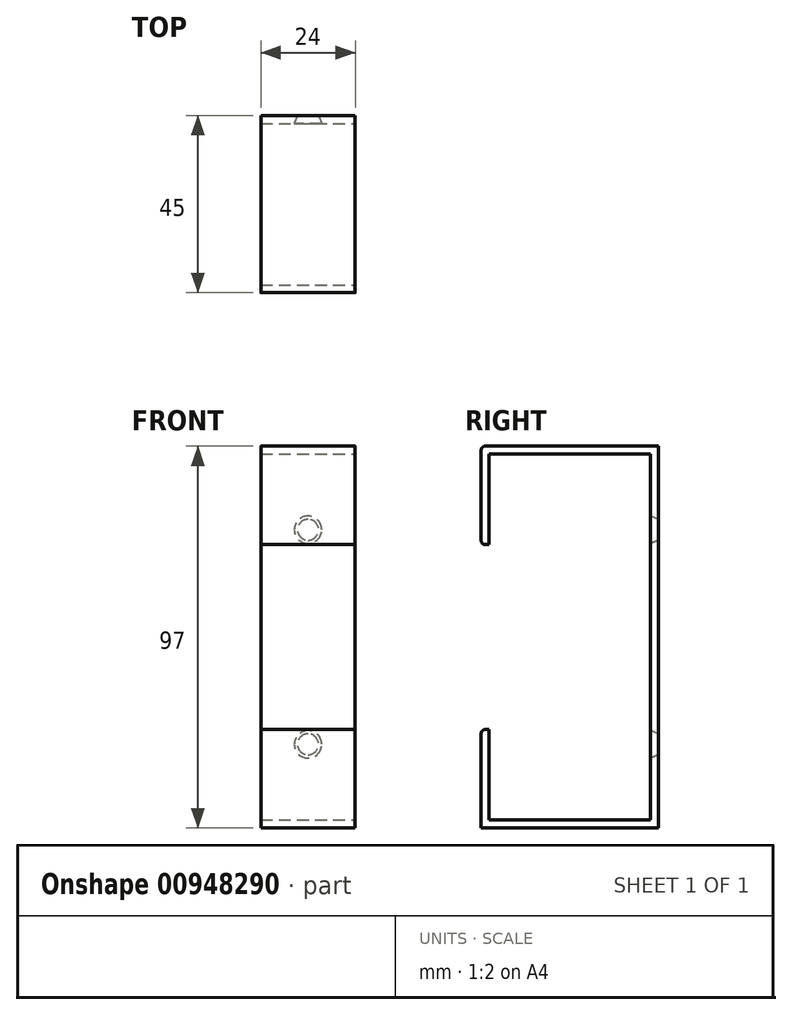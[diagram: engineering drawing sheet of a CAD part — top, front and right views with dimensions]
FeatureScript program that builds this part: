
annotation { "Feature Type Name" : "Feature", "Feature Type Description" : "" }
export const myFeature = defineFeature(function(context is Context, id is Id, definition is map)
    precondition{}
    {
        {
            var Q0;
            Q0=qCreatedBy(makeId("Top.planeOp"),FACE);
            var sketch = newSketch(context, id + "F0", { "sketchPlane" : qUnion([Q0])});
            skLineSegment(sketch, "E0.bottom", {"start": v(-14.15, 20.5) * mm, "end": v(7.85, 20.5) * mm});
            skLineSegment(sketch, "E0.top", {"start": v(-14.15, -20.5) * mm, "end": v(7.85, -20.5) * mm});
            skLineSegment(sketch, "E0.left", {"start": v(-14.15, 20.5) * mm, "end": v(-14.15, -20.5) * mm});
            skLineSegment(sketch, "E0.right", {"start": v(7.85, 20.5) * mm, "end": v(7.85, -20.5) * mm});
            skLineSegment(sketch, "E1.0", {"start": v(-14.15, 22.5) * mm, "end": v(7.85, 22.5) * mm});
            skLineSegment(sketch, "E2", {"start": v(-14.15, 22.5) * mm, "end": v(-14.15, 20.5) * mm});
            skLineSegment(sketch, "E3.0", {"start": v(9.85, 20.5) * mm, "end": v(9.85, -20.5) * mm});
            skLineSegment(sketch, "E4", {"start": v(7.85, 22.5) * mm, "end": v(9.85, 22.5) * mm});
            skLineSegment(sketch, "E5", {"start": v(9.85, 22.5) * mm, "end": v(9.85, 20.5) * mm});
            skLineSegment(sketch, "E6.0", {"start": v(-14.15, -22.5) * mm, "end": v(7.85, -22.5) * mm});
            skLineSegment(sketch, "E7", {"start": v(-14.15, -20.5) * mm, "end": v(-14.15, -22.5) * mm});
            skLineSegment(sketch, "E8", {"start": v(7.85, -22.5) * mm, "end": v(9.85, -22.5) * mm});
            skLineSegment(sketch, "E9", {"start": v(9.85, -22.5) * mm, "end": v(9.85, -20.5) * mm});
            skLineSegment(sketch, "E10", {"start": v(7.85, 20.5) * mm, "end": v(9.85, 20.5) * mm});
            skLineSegment(sketch, "E11", {"start": v(7.85, -20.5) * mm, "end": v(9.85, -20.5) * mm});
            skSolve(sketch);
        }
        {
            var Q0;
            Q0=makeQuery(id+"F0.imprint","IMPRINT",FACE,{"disambiguationData":[TD([[makeQuery(id+"F0.imprint","IMPRINT",EDGE,{"derivedFrom":sQuery(id+"F0.wireOp",EDGE,"E0.bottom")}),-1.0]])]});
            var Q1;
            Q1=makeQuery(id+"F0.imprint","IMPRINT",FACE,{"disambiguationData":[TD([[makeQuery(id+"F0.imprint","IMPRINT",EDGE,{"derivedFrom":sQuery(id+"F0.wireOp",EDGE,"E0.right")}),1.0]])]});
            extrude(context, id + "F1", {"entities" : qUnion([Q0, Q1]), "depth" : 2 * mm, "offsetDistance" : 25 * mm});
        }
        {
            var Q0;
            Q0=makeQuery(id+"F0.imprint","IMPRINT",FACE,{"disambiguationData":[TD([[makeQuery(id+"F0.imprint","IMPRINT",EDGE,{"derivedFrom":sQuery(id+"F0.wireOp",EDGE,"E0.bottom")}),1.0]])]});
            extrude(context, id + "F2", {"entities" : qUnion([Q0]), "operationType" : NewBodyOperationType.ADD, "depth" : 97 * mm, "offsetDistance" : 25 * mm});
        }
        {
            var Q0;
            Q0=makeQuery(id+"F2.opExtrude","SWEPT_FACE",FACE,{"disambiguationData":[OSD([sQuery(id+"F0.wireOp",EDGE,"E0.bottom"),sQuery(id+"F0.wireOp",EDGE,"E10")])]});
            var sketch = newSketch(context, id + "F3", { "sketchPlane" : qUnion([Q0])});
            skLineSegment(sketch, "E12.bottom", {"start": v(-14.15, 97) * mm, "end": v(9.85, 97) * mm});
            skLineSegment(sketch, "E12.top", {"start": v(-14.15, 95) * mm, "end": v(9.85, 95) * mm});
            skLineSegment(sketch, "E12.left", {"start": v(-14.15, 97) * mm, "end": v(-14.15, 95) * mm});
            skLineSegment(sketch, "E12.right", {"start": v(9.85, 97) * mm, "end": v(9.85, 95) * mm});
            skSolve(sketch);
        }
        {
            var Q0;
            Q0=makeQuery(id+"F3.imprint","IMPRINT",FACE,{"disambiguationData":[TD([[makeQuery(id+"F3.imprint","IMPRINT",EDGE,{"derivedFrom":sQuery(id+"F3.wireOp",EDGE,"E12.bottom")}),-1.0]])]});
            var Q1;
            Q1=makeQuery(id+"F1.opExtrude","SWEPT_FACE",FACE,{"disambiguationData":[OSD([sQuery(id+"F0.wireOp",EDGE,"E0.top"),sQuery(id+"F0.wireOp",EDGE,"E11")])]});
            extrude(context, id + "F4", {"entities" : qUnion([Q0]), "operationType" : NewBodyOperationType.ADD, "depth" : 41 * mm, "endBoundEntityFace" : qUnion([Q1]), "offsetDistance" : 25 * mm});
        }
        {
            var Q0;
            Q0=makeQuery(id+"F4.boolean.opBoolean","MERGE",FACE,{"derivedFrom":[makeQuery(id+"F2.opExtrude","CAP_FACE",FACE,{"disambiguationData":[OSD([sQuery(id+"F0.wireOp",EDGE,"E0.bottom"),sQuery(id+"F0.wireOp",EDGE,"E1.0"),sQuery(id+"F0.wireOp",EDGE,"E2"),sQuery(id+"F0.wireOp",EDGE,"E4"),sQuery(id+"F0.wireOp",EDGE,"E5"),sQuery(id+"F0.wireOp",EDGE,"E10")])],"isStart":false}),makeQuery(id+"F4.opExtrude","SWEPT_FACE",FACE,{"disambiguationData":[OSD([sQuery(id+"F3.wireOp",EDGE,"E12.bottom")])]})]});
            var sketch = newSketch(context, id + "F5", { "sketchPlane" : qUnion([Q0])});
            skLineSegment(sketch, "E13.bottom", {"start": v(-14.15, -20.5) * mm, "end": v(0, -20.5) * mm});
            skLineSegment(sketch, "E13.top", {"start": v(-14.15, -22.5) * mm, "end": v(9.85, -22.5) * mm});
            skLineSegment(sketch, "E13.left", {"start": v(-14.15, -22.5) * mm, "end": v(-14.15, -20.5) * mm});
            skLineSegment(sketch, "E13.right", {"start": v(9.85, -22.5) * mm, "end": v(9.85, -20.5) * mm});
            skSolve(sketch);
        }
        {
            var Q0;
            Q0=makeQuery(id+"F0.imprint","IMPRINT",FACE,{"disambiguationData":[TD([[makeQuery(id+"F0.imprint","IMPRINT",EDGE,{"derivedFrom":sQuery(id+"F0.wireOp",EDGE,"E0.top")}),-1.0]])]});
            extrude(context, id + "F6", {"entities" : qUnion([Q0]), "operationType" : NewBodyOperationType.ADD, "depth" : 25 * mm, "offsetDistance" : 25 * mm});
        }
        {
            var Q0;
            {var subQ1=sQuery(id+"F5.wireOp",EDGE,"E13.bottom");Q0=makeQuery(id+"F5.imprint","IMPRINT",FACE,{"disambiguationData":[TD([[makeQuery(id+"F5.imprint","IMPRINT",EDGE,{"derivedFrom":subQ1}),-1.0]])]});}
            extrude(context, id + "F7", {"entities" : qUnion([Q0]), "operationType" : NewBodyOperationType.ADD, "oppositeDirection" : true, "depth" : 25 * mm, "offsetDistance" : 25 * mm});
        }
        {
            var Q0;
            Q0=makeQuery(id+"F6.opExtrude","CAP_EDGE",EDGE,{"disambiguationData":[OSD([sQuery(id+"F0.wireOp",EDGE,"E6.0"),sQuery(id+"F0.wireOp",EDGE,"E8")])],"isStart":false});
            var Q1;
            Q1=makeQuery(id+"F7.opExtrude","CAP_EDGE",EDGE,{"disambiguationData":[OSD([sQuery(id+"F5.wireOp",EDGE,"E13.top")])],"isStart":false});
            var Q2;
            Q2=makeQuery(id+"F7.opExtrude","CAP_EDGE",EDGE,{"disambiguationData":[OSD([sQuery(id+"F5.wireOp",EDGE,"E13.top")])],"isStart":true});
            fillet(context, id + "F8", {"entities" : qUnion([Q0, Q1, Q2]), "radius" : 1 * mm, "tangentPropagation" : true, "allowEdgeOverflow" : false});
        }
        {
            var Q0;
            Q0=makeQuery(id+"F2.opExtrude","SWEPT_FACE",FACE,{"disambiguationData":[OSD([sQuery(id+"F0.wireOp",EDGE,"E0.bottom"),sQuery(id+"F0.wireOp",EDGE,"E10")])]});
            var sketch = newSketch(context, id + "F9", { "sketchPlane" : qUnion([Q0])});
            skLineSegment(sketch, "E14", {"start": v(-2.15, 95) * mm, "end": v(-2.15, 2) * mm});
            skLineSegment(sketch, "E15.bottom", {"start": v(2.6, 21.24) * mm, "end": v(-6.9, 21.24) * mm});
            skLineSegment(sketch, "E15.top", {"start": v(2.6, 75.76) * mm, "end": v(-6.9, 75.76) * mm});
            skLineSegment(sketch, "E15.left", {"start": v(2.6, 21.24) * mm, "end": v(2.6, 75.76) * mm});
            skLineSegment(sketch, "E15.right", {"start": v(-6.9, 21.24) * mm, "end": v(-6.9, 75.76) * mm});
            skPoint(sketch, "E15.middle", {"position": v(-2.15, 48.5) * mm});
            skCircle(sketch, "E16", {"center": v(-2.15, 75.76) * mm, "radius": 1.91 * mm});
            skCircle(sketch, "E17", {"center": v(-2.15, 21.24) * mm, "radius": 2.63 * mm});
            skSolve(sketch);
        }
        {
            var Q0;
            Q0=sQuery(id+"F9.wireOp",VERTEX,"E16.center");
            var Q1;
            Q1=sQuery(id+"F9.wireOp",VERTEX,"E17.center");
            var Q2;
            Q2=makeQuery(id+"F1.opExtrude","SWEPT_BODY",BODY,{"disambiguationData":[OSD([sQuery(id+"F0.wireOp",EDGE,"E0.bottom"),sQuery(id+"F0.wireOp",EDGE,"E0.top"),sQuery(id+"F0.wireOp",EDGE,"E0.left"),sQuery(id+"F0.wireOp",EDGE,"E3.0"),sQuery(id+"F0.wireOp",EDGE,"E10"),sQuery(id+"F0.wireOp",EDGE,"E11")])]});
            hole(context, id + "F10", {"style" : HoleStyle.C_SINK, "endStyle" : HoleEndStyle.THROUGH, "holeDiameter" : 5 * mm, "cSinkDiameter" : 7 * mm, "cSinkAngle" : 45 * degree, "majorDiameter" : 5 * mm, "isTappedThrough" : true, "tappedDepth" : 12 * mm, "tapClearance" : 3, "locations" : qUnion([Q0, Q1]), "scope" : qUnion([Q2])});
        }
    });
